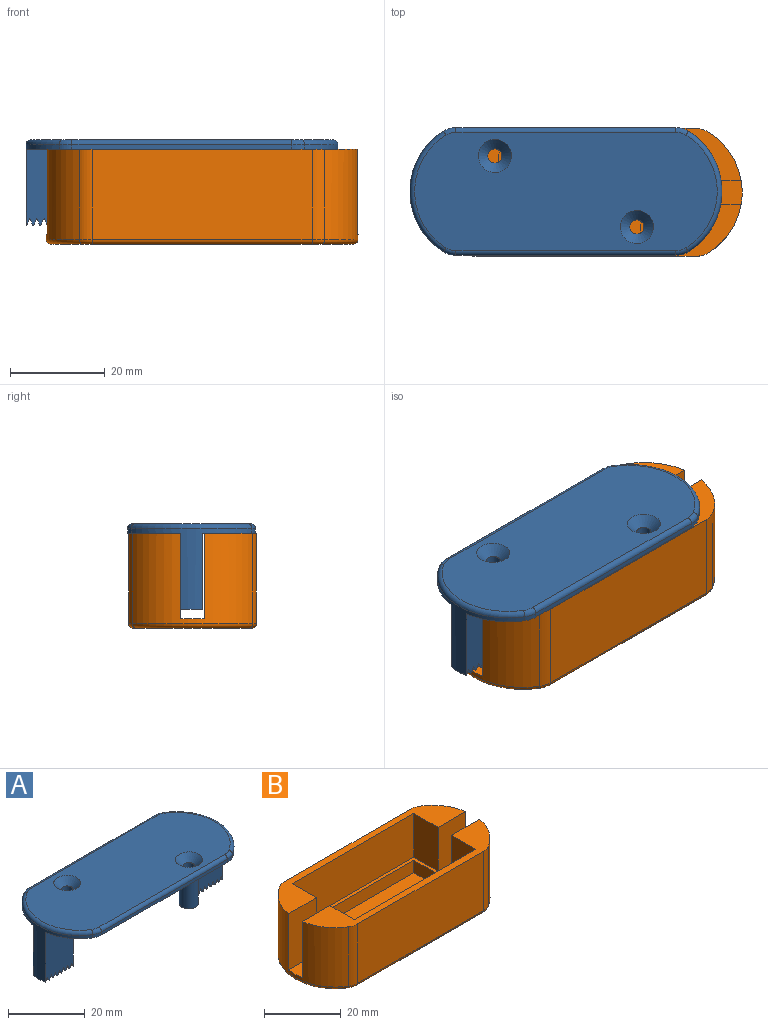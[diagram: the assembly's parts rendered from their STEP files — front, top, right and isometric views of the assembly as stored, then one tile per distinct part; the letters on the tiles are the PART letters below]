
ASSEMBLY  parts=2 mates=1
PART A: 74 faces, bbox 68.4x27.8x18 mm
  f0: plane 15.97x4.6mm, normal (1,0,0), area 73.4mm2, adj f1,f21,f22,f68
  f1: plane 16x10.28mm, normal (0,-1,0), area 158.4mm2, adj f0,f2,f3,f4,f5,f6,f7,f18
  f2: plane 4.6x0.2mm, normal (0,0,-1), area 0.9mm2, adj f1,f22,f61,f70
  f3: plane 4.6x0.2mm, normal (0,0,-1), area 0.9mm2, adj f1,f22,f66,f69
  f4: plane 4.6x0.2mm, normal (0,0,-1), area 0.9mm2, adj f1,f22,f64,f67
  f5: plane 4.6x0.2mm, normal (0,0,-1), area 0.9mm2, adj f1,f22,f62,f65
  f6: plane 4.6x0.2mm, normal (0,0,-1), area 0.9mm2, adj f1,f22,f60,f63
  f7: plane 4.6x0.2mm, normal (0,0,-1), area 0.9mm2, adj f1,f22,f58,f71
  f8: plane 15.97x4.6mm, normal (-1,0,0), area 73.4mm2, adj f21,f24,f25,f55
  f9: plane 4.6x0.18mm, normal (0,0,-1), area 0.5mm2, adj f20,f56
  f10: plane 4.6x0.2mm, normal (0,0,-1), area 0.9mm2, adj f24,f25,f53,f54
  f11: plane 4.6x0.2mm, normal (0,0,-1), area 0.9mm2, adj f24,f25,f51,f52
  f12: plane 4.6x0.2mm, normal (0,0,-1), area 0.9mm2, adj f24,f25,f49,f50
  f13: plane 4.6x0.2mm, normal (0,0,-1), area 0.9mm2, adj f24,f25,f47,f48
  f14: plane 4.6x0.2mm, normal (0,0,-1), area 0.9mm2, adj f24,f25,f45,f46
  f15: plane 4.6x0.2mm, normal (0,0,-1), area 0.9mm2, adj f24,f25,f44,f57
  f16: plane 63.92x25mm, normal (0,0,1), area 1411mm2, adj f32,f33,f34,f35,f37,f39,f41,f43
  f17: plane 46.46x1mm, normal (0,1,0), area 46.5mm2, adj f21,f34,f36,f40
  f18: cylinder r=15mm len=25.5mm, axis (0,0,-1), area 104.4mm2, adj f1,f21,f22,f23,f32,f40,f42
  f19: plane 46.46x1mm, normal (0,-1,0), area 46.5mm2, adj f21,f33,f38,f42
  f20: cylinder r=15mm len=25.5mm, axis (0,0,-1), area 104.4mm2, adj f9,f21,f24,f25,f35,f36,f38
  f21: plane 65.57x27mm, normal (0,0,-1), area 1514.8mm2, adj f0,f1,f8,f17,f18,f19,f20,f22
  f22: plane 16x10.28mm, normal (0,1,0), area 158.4mm2, adj f0,f2,f3,f4,f5,f6,f7,f18
  f23: plane 4.6x0.18mm, normal (0,0,-1), area 0.5mm2, adj f18,f59
  f24: plane 16x10.28mm, normal (0,-1,0), area 158.4mm2, adj f8,f10,f11,f12,f13,f14,f15,f20
  f25: plane 16x10.28mm, normal (0,1,0), area 158.4mm2, adj f8,f10,f11,f12,f13,f14,f15,f20
  f26: cylinder r=2.5mm len=12mm, axis (0,0,1), area 188.5mm2, adj f21,f28
  f27: cylinder r=1.5mm len=12mm, axis (0,0,1), area 113.1mm2, adj f28,f73
  f28: plane 5x5mm, normal (0,0,-1), area 12.6mm2, adj f26,f27
  f29: cylinder r=2.5mm len=12mm, axis (0,0,1), area 188.5mm2, adj f21,f31
  f30: cylinder r=1.5mm len=12mm, axis (0,0,1), area 113.1mm2, adj f31,f72
  f31: plane 5x5mm, normal (0,0,-1), area 12.6mm2, adj f29,f30
  f32: torus R=14mm, axis (0,0,1), area 46.7mm2, adj f16,f18,f41,f43
  f33: cylinder r=1mm len=46.46mm, axis (-1,0,0), area 73mm2, adj f16,f19,f39,f43
  f34: cylinder r=1mm len=46.46mm, axis (1,0,0), area 73mm2, adj f16,f17,f37,f41
  f35: torus R=14mm, axis (0,0,1), area 46.7mm2, adj f16,f20,f37,f39
  f36: cylinder r=5mm len=2.63mm, axis (0,0,-1), area 2.8mm2, adj f17,f20,f21,f37
  f37: torus R=4mm, axis (0,0,1), area 4mm2, adj f16,f34,f35,f36
  f38: cylinder r=5mm len=2.63mm, axis (0,0,-1), area 2.8mm2, adj f19,f20,f21,f39
  f39: torus R=4mm, axis (0,0,1), area 4mm2, adj f16,f33,f35,f38
  f40: cylinder r=5mm len=2.63mm, axis (0,0,-1), area 2.8mm2, adj f17,f18,f21,f41
  f41: torus R=4mm, axis (0,0,1), area 4mm2, adj f16,f32,f34,f40
  f42: cylinder r=5mm len=2.63mm, axis (0,0,-1), area 2.8mm2, adj f18,f19,f21,f43
  f43: torus R=4mm, axis (0,0,1), area 4mm2, adj f16,f32,f33,f42
  f44: plane 4.6x1.35mm, normal (-0.9,0,-0.43), area 6.9mm2, adj f15,f24,f25,f45
  f45: plane 4.6x1.35mm, normal (0.9,0,-0.43), area 6.9mm2, adj f14,f24,f25,f44
  f46: plane 4.6x1.35mm, normal (-0.9,0,-0.43), area 6.9mm2, adj f14,f24,f25,f47
  f47: plane 4.6x1.35mm, normal (0.9,0,-0.43), area 6.9mm2, adj f13,f24,f25,f46
  f48: plane 4.6x1.35mm, normal (-0.9,0,-0.43), area 6.9mm2, adj f13,f24,f25,f49
  f49: plane 4.6x1.35mm, normal (0.9,0,-0.43), area 6.9mm2, adj f12,f24,f25,f48
  f50: plane 4.6x1.35mm, normal (-0.9,0,-0.43), area 6.9mm2, adj f12,f24,f25,f51
  f51: plane 4.6x1.35mm, normal (0.9,0,-0.43), area 6.9mm2, adj f11,f24,f25,f50
  f52: plane 4.6x1.35mm, normal (-0.9,0,-0.43), area 6.9mm2, adj f11,f24,f25,f53
  f53: plane 4.6x1.35mm, normal (0.9,0,-0.43), area 6.9mm2, adj f10,f24,f25,f52
  f54: plane 4.6x1.35mm, normal (-0.9,0,-0.43), area 6.9mm2, adj f10,f24,f25,f55
  f55: plane 4.6x1.32mm, normal (0.9,0,-0.43), area 6.7mm2, adj f8,f24,f25,f54
  f56: plane 4.6x1.35mm, normal (-0.9,0,-0.43), area 6.9mm2, adj f9,f24,f25,f57
  f57: plane 4.6x1.35mm, normal (0.9,0,-0.43), area 6.9mm2, adj f15,f24,f25,f56
  f58: plane 4.6x1.35mm, normal (-0.9,0,-0.43), area 6.9mm2, adj f1,f7,f22,f59
  f59: plane 4.6x1.35mm, normal (0.9,0,-0.43), area 6.9mm2, adj f1,f22,f23,f58
  f60: plane 4.6x1.35mm, normal (-0.9,0,-0.43), area 6.9mm2, adj f1,f6,f22,f61
  f61: plane 4.6x1.35mm, normal (0.9,0,-0.43), area 6.9mm2, adj f1,f2,f22,f60
  f62: plane 4.6x1.35mm, normal (-0.9,0,-0.43), area 6.9mm2, adj f1,f5,f22,f63
  f63: plane 4.6x1.35mm, normal (0.9,0,-0.43), area 6.9mm2, adj f1,f6,f22,f62
  f64: plane 4.6x1.35mm, normal (-0.9,0,-0.43), area 6.9mm2, adj f1,f4,f22,f65
  f65: plane 4.6x1.35mm, normal (0.9,0,-0.43), area 6.9mm2, adj f1,f5,f22,f64
  f66: plane 4.6x1.35mm, normal (-0.9,0,-0.43), area 6.9mm2, adj f1,f3,f22,f67
  f67: plane 4.6x1.35mm, normal (0.9,0,-0.43), area 6.9mm2, adj f1,f4,f22,f66
  f68: plane 4.6x1.32mm, normal (-0.9,0,-0.43), area 6.7mm2, adj f0,f1,f22,f69
  f69: plane 4.6x1.35mm, normal (0.9,0,-0.43), area 6.9mm2, adj f1,f3,f22,f68
  f70: plane 4.6x1.35mm, normal (-0.9,0,-0.43), area 6.9mm2, adj f1,f2,f22,f71
  f71: plane 4.6x1.35mm, normal (0.9,0,-0.43), area 6.9mm2, adj f1,f7,f22,f70
  f72: cone r=1.5mm half-angle=45deg, axis (0,0,1), area 44.4mm2, adj f16,f30
  f73: cone r=1.5mm half-angle=45deg, axis (0,0,1), area 44.4mm2, adj f16,f27
PART B: 48 faces, bbox 68.4x27.8x20 mm
  f0: plane 65.92x21mm, normal (0,0,1), area 942.4mm2, adj f1,f2,f6,f7,f8,f9,f10,f11
  f1: plane 34.7x4mm, normal (0,1,0), area 138.8mm2, adj f0,f18,f19,f47
  f2: plane 4.7x4mm, normal (0,-1,0), area 18.8mm2, adj f0,f10,f13,f46
  f3: plane 63.92x25mm, normal (0,0,-1), area 1462.8mm2, adj f30,f32,f34,f35,f36,f37,f39,f41
  f4: cylinder r=1.5mm len=3mm, axis (0,0,-1), area 18.8mm2, adj f13,f33
  f5: cylinder r=1.5mm len=3mm, axis (0,0,-1), area 18.8mm2, adj f19,f31
  f6: cylinder r=15mm len=25.5mm, axis (0,0,-1), area 488.7mm2, adj f0,f12,f16,f24,f29,f36,f38,f42
  f7: cylinder r=15mm len=25.5mm, axis (0,0,-1), area 488.7mm2, adj f0,f9,f15,f24,f29,f35,f40,f44
  f8: plane 34.7x4mm, normal (0,-1,0), area 138.8mm2, adj f0,f11,f13,f46
  f9: plane 18x11.25mm, normal (0,-1,0), area 188.5mm2, adj f0,f7,f10,f13,f22,f24
  f10: plane 8x4mm, normal (1,0,0), area 32mm2, adj f0,f2,f9,f13
  f11: plane 8x4mm, normal (-1,0,0), area 32mm2, adj f0,f8,f12,f13
  f12: plane 18x11.25mm, normal (0,-1,0), area 188.5mm2, adj f0,f6,f11,f13,f21,f24
  f13: plane 45x9mm, normal (0,0,1), area 91.2mm2, adj f2,f4,f8,f9,f10,f11,f12,f20
  f14: plane 4.7x4mm, normal (0,1,0), area 18.8mm2, adj f0,f17,f19,f47
  f15: plane 18x11.25mm, normal (0,1,0), area 188.5mm2, adj f0,f7,f18,f19,f26,f29
  f16: plane 18x11.25mm, normal (0,1,0), area 188.5mm2, adj f0,f6,f17,f19,f27,f29
  f17: plane 8x4mm, normal (-1,0,0), area 32mm2, adj f0,f14,f16,f19
  f18: plane 8x4mm, normal (1,0,0), area 32mm2, adj f0,f1,f15,f19
  f19: plane 45x9mm, normal (0,0,1), area 91.2mm2, adj f1,f5,f14,f15,f16,f17,f18,f25
  f20: plane 45x14mm, normal (0,-1,0), area 630mm2, adj f13,f21,f22,f24
  f21: plane 14x9mm, normal (-1,0,0), area 126mm2, adj f12,f13,f20,f24
  f22: plane 14x9mm, normal (1,0,0), area 126mm2, adj f9,f13,f20,f24
  f23: plane 46.46x19mm, normal (0,1,0), area 882.7mm2, adj f24,f34,f38,f40
  f24: plane 65.5x11mm, normal (0,0,1), area 255.4mm2, adj f6,f7,f9,f12,f20,f21,f22,f23
  f25: plane 45x14mm, normal (0,1,0), area 630mm2, adj f19,f26,f27,f29
  f26: plane 14x9mm, normal (1,0,0), area 126mm2, adj f15,f19,f25,f29
  f27: plane 14x9mm, normal (-1,0,0), area 126mm2, adj f16,f19,f25,f29
  f28: plane 46.46x19mm, normal (0,-1,0), area 882.7mm2, adj f29,f37,f42,f44
  f29: plane 65.5x11mm, normal (0,0,1), area 255.4mm2, adj f6,f7,f15,f16,f25,f26,f27,f28
  f30: cylinder r=2mm len=4mm, axis (0,0,-1), area 50.3mm2, adj f3,f31
  f31: plane 4x4mm, normal (0,0,-1), area 5.5mm2, adj f5,f30
  f32: cylinder r=2mm len=4mm, axis (0,0,-1), area 50.3mm2, adj f3,f33
  f33: plane 4x4mm, normal (0,0,-1), area 5.5mm2, adj f4,f32
  f34: cylinder r=1mm len=46.46mm, axis (-1,0,0), area 73mm2, adj f3,f23,f39,f41
  f35: torus R=14mm, axis (0,0,1), area 46.7mm2, adj f3,f7,f41,f45
  f36: torus R=14mm, axis (0,0,1), area 46.7mm2, adj f3,f6,f39,f43
  f37: cylinder r=1mm len=46.46mm, axis (1,0,0), area 73mm2, adj f3,f28,f43,f45
  f38: cylinder r=5mm len=19mm, axis (0,0,-1), area 52.7mm2, adj f6,f23,f24,f39
  f39: torus R=4mm, axis (0,0,1), area 4mm2, adj f3,f34,f36,f38
  f40: cylinder r=5mm len=19mm, axis (0,0,-1), area 52.7mm2, adj f7,f23,f24,f41
  f41: torus R=4mm, axis (0,0,1), area 4mm2, adj f3,f34,f35,f40
  f42: cylinder r=5mm len=19mm, axis (0,0,-1), area 52.7mm2, adj f6,f28,f29,f43
  f43: torus R=4mm, axis (0,0,1), area 4mm2, adj f3,f36,f37,f42
  f44: cylinder r=5mm len=19mm, axis (0,0,-1), area 52.7mm2, adj f7,f28,f29,f45
  f45: torus R=4mm, axis (0,0,1), area 4mm2, adj f3,f35,f37,f44
  f46: cylinder r=3.5mm len=7mm, axis (0,0,-1), area 72.8mm2, adj f0,f2,f8,f13
  f47: cylinder r=3.5mm len=7mm, axis (0,0,-1), area 72.8mm2, adj f0,f1,f14,f19
PLACE A t=(-0.5,0,-25)mm
PLACE B t=(3.76,-0.2,0)mm
MATE slider A.f15 <-> B.f0  axis (0,0,-1) through (30.88,2.3,4)mm
